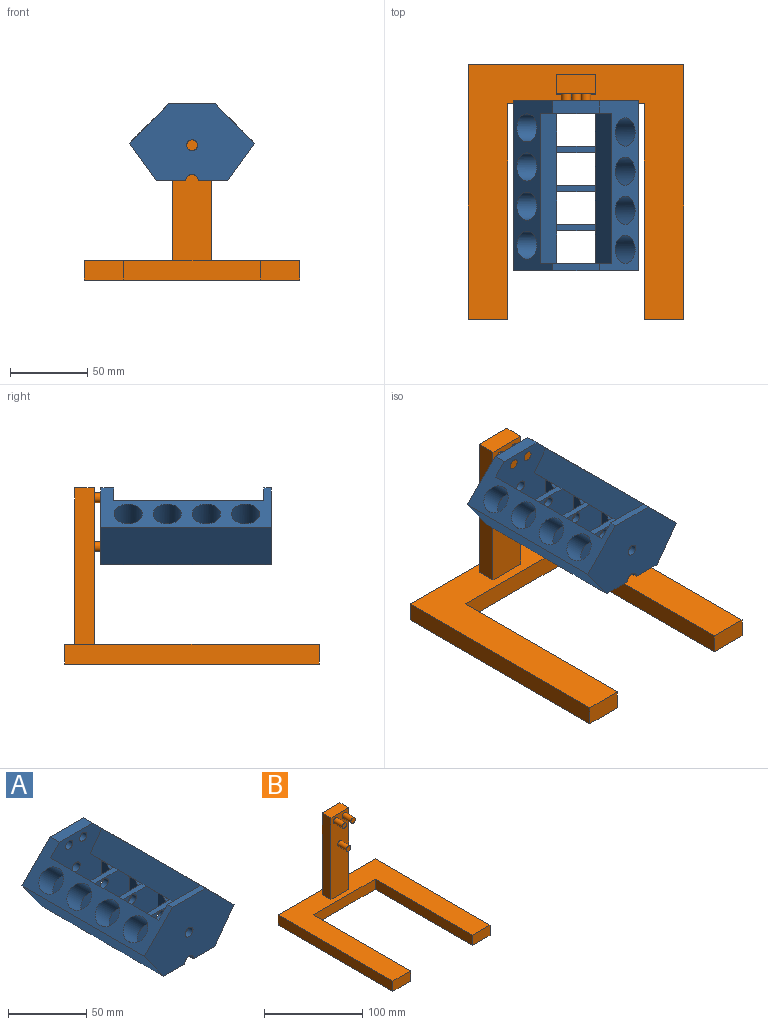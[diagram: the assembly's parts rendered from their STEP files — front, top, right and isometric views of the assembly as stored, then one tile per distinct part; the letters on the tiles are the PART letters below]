
ASSEMBLY  parts=2 mates=1
PART A: 64 faces, bbox 81.3x110.5x49.8 mm
  f0: plane 21.34x16.54mm, normal (-1,0,0), area 298.5mm2, adj f7,f11,f17,f51,f54
  f1: plane 21.34x16.54mm, normal (-1,0,0), area 298.5mm2, adj f8,f13,f17,f49,f56
  f2: plane 21.34x16.54mm, normal (-1,0,0), area 298.5mm2, adj f9,f10,f17,f52,f53
  f3: plane 21.34x16.54mm, normal (1,0,0), area 298.5mm2, adj f7,f11,f28,f47,f58
  f4: plane 21.34x16.54mm, normal (1,0,0), area 298.5mm2, adj f8,f13,f28,f45,f60
  f5: plane 21.34x16.54mm, normal (1,0,0), area 298.5mm2, adj f9,f10,f28,f48,f57
  f6: plane 49.81x46.33mm, normal (0,1,0), area 1910.8mm2, adj f14,f15,f17,f24,f25,f26,f27,f28
  f7: plane 46.33x27.08mm, normal (0,1,0), area 1077.7mm2, adj f0,f3,f17,f21,f28,f34,f39,f44
  f8: plane 46.33x27.08mm, normal (0,1,0), area 1077.7mm2, adj f1,f4,f17,f19,f28,f32,f37,f41
  f9: plane 46.33x27.08mm, normal (0,1,0), area 1077.7mm2, adj f2,f5,f17,f20,f28,f30,f35,f40
  f10: plane 46.33x27.08mm, normal (0,-1,0), area 1077.7mm2, adj f2,f5,f17,f19,f28,f32,f37,f41
  f11: plane 46.33x27.08mm, normal (0,-1,0), area 1077.7mm2, adj f0,f3,f17,f20,f28,f30,f35,f40
  f12: plane 46.33x27.08mm, normal (0,-1,0), area 1077.7mm2, adj f17,f21,f24,f27,f28,f34,f39,f44
  f13: plane 49.81x46.33mm, normal (0,-1,0), area 1815.8mm2, adj f1,f4,f14,f15,f17,f18,f22,f28
  f14: plane 110.49x25.61mm, normal (-0.71,0,0.71), area 1829mm2, adj f6,f13,f16,f22,f23,f25,f28,f42
  f15: plane 110.49x25.61mm, normal (0.71,0,0.71), area 1829mm2, adj f6,f13,f16,f22,f23,f25,f29,f43
  f16: plane 81.28x49.81mm, normal (0,-1,0), area 2904mm2, adj f14,f15,f17,f25,f26,f28,f29,f31
  f17: plane 110.49x19.1mm, normal (0,0,-1), area 480.3mm2, adj f0,f1,f2,f6,f7,f8,f9,f10
  f18: plane 19.1x8.38mm, normal (0,0,-1), area 160.1mm2, adj f13,f23,f28,f33
  f19: plane 19.1x4.06mm, normal (0,0,-1), area 77.6mm2, adj f8,f10,f28,f32
  f20: plane 19.1x4.06mm, normal (0,0,-1), area 77.6mm2, adj f9,f11,f28,f30
  f21: plane 19.1x4.06mm, normal (0,0,-1), area 77.6mm2, adj f7,f12,f28,f34
  f22: plane 30.06x8.38mm, normal (0,0,1), area 251.9mm2, adj f13,f14,f15,f23
  f23: plane 81.28x49.81mm, normal (0,1,0), area 2809mm2, adj f14,f15,f17,f18,f22,f28,f29,f33
  f24: plane 21.34x16.54mm, normal (-1,0,0), area 298.5mm2, adj f6,f12,f17,f50,f55
  f25: plane 30.06x4.57mm, normal (0,0,1), area 137.4mm2, adj f6,f14,f15,f16
  f26: plane 19.1x4.57mm, normal (0,0,-1), area 87.3mm2, adj f6,f16,f28,f31
  f27: plane 21.34x16.54mm, normal (1,0,0), area 298.5mm2, adj f6,f12,f28,f46,f59
  f28: plane 110.49x24.2mm, normal (-0.81,0,-0.59), area 3297.9mm2, adj f3,f4,f5,f6,f7,f8,f9,f10
  f29: plane 110.49x24.2mm, normal (0.81,0,-0.59), area 3297.9mm2, adj f15,f16,f17,f23
  f30: cylinder r=4.06mm len=8.13mm, axis (0,-1,0), area 51.9mm2, adj f9,f11,f17,f20
  f31: cylinder r=4.06mm len=8.13mm, axis (0,-1,0), area 58.4mm2, adj f6,f16,f17,f26
  f32: cylinder r=4.06mm len=8.13mm, axis (0,-1,0), area 51.9mm2, adj f8,f10,f17,f19
  f33: cylinder r=4.06mm len=8.38mm, axis (0,-1,0), area 107mm2, adj f13,f17,f18,f23
  f34: cylinder r=4.06mm len=8.13mm, axis (0,-1,0), area 51.9mm2, adj f7,f12,f17,f21
  f35: cylinder r=3.56mm len=7.11mm, axis (0,-1,0), area 90.8mm2, adj f9,f11
  f36: cylinder r=3.56mm len=7.11mm, axis (0,-1,0), area 102.2mm2, adj f6,f16
  f37: cylinder r=3.56mm len=7.11mm, axis (0,-1,0), area 90.8mm2, adj f8,f10
  f38: cylinder r=3.56mm len=8.38mm, axis (0,-1,0), area 187.3mm2, adj f13,f23
  f39: cylinder r=3.56mm len=7.11mm, axis (0,-1,0), area 90.8mm2, adj f7,f12
  f40: plane 25.25x4.06mm, normal (0,0,1), area 102.6mm2, adj f9,f11,f42,f43
  f41: plane 25.25x4.06mm, normal (0,0,1), area 102.6mm2, adj f8,f10,f42,f43
  f42: plane 97.54x14.6mm, normal (0.81,0,0.59), area 1756mm2, adj f6,f13,f14,f40,f41,f44,f45,f46
  f43: plane 97.54x14.6mm, normal (-0.81,0,0.59), area 1756.1mm2, adj f6,f13,f15,f40,f41,f44,f49,f50
  f44: plane 25.25x4.06mm, normal (0,0,1), area 102.6mm2, adj f7,f12,f42,f43
  f45: plane 21.34x10.54mm, normal (0.71,0,-0.71), area 93.8mm2, adj f4,f8,f13,f42,f60
  f46: plane 21.34x10.54mm, normal (0.71,0,-0.71), area 93.8mm2, adj f6,f12,f27,f42,f59
  f47: plane 21.34x10.54mm, normal (0.71,0,-0.71), area 93.8mm2, adj f3,f7,f11,f42,f58
  f48: plane 21.34x10.54mm, normal (0.71,0,-0.71), area 93.8mm2, adj f5,f9,f10,f42,f57
  f49: plane 21.34x10.54mm, normal (-0.71,0,-0.71), area 93.8mm2, adj f1,f8,f13,f43,f56
  f50: plane 21.34x10.54mm, normal (-0.71,0,-0.71), area 93.8mm2, adj f6,f12,f24,f43,f55
  f51: plane 21.34x10.54mm, normal (-0.71,0,-0.71), area 93.8mm2, adj f0,f7,f11,f43,f54
  f52: plane 21.34x10.54mm, normal (-0.71,0,-0.71), area 93.8mm2, adj f2,f9,f10,f43,f53
  f53: cylinder r=9.14mm len=28.14mm, axis (0.71,0,0.71), area 1063.1mm2, adj f2,f15,f52
  f54: cylinder r=9.14mm len=28.14mm, axis (0.71,0,0.71), area 1063.1mm2, adj f0,f15,f51
  f55: cylinder r=9.14mm len=28.14mm, axis (0.71,0,0.71), area 1063.1mm2, adj f15,f24,f50
  f56: cylinder r=9.14mm len=28.14mm, axis (0.71,0,0.71), area 1063.1mm2, adj f1,f15,f49
  f57: cylinder r=9.14mm len=28.14mm, axis (-0.71,0,0.71), area 1063.1mm2, adj f5,f14,f48
  f58: cylinder r=9.14mm len=28.14mm, axis (-0.71,0,0.71), area 1063.1mm2, adj f3,f14,f47
  f59: cylinder r=9.14mm len=28.14mm, axis (-0.71,0,0.71), area 1063.1mm2, adj f14,f27,f46
  f60: cylinder r=9.14mm len=28.14mm, axis (-0.71,0,0.71), area 1063.1mm2, adj f4,f14,f45
  f61: cylinder r=3.17mm len=8.38mm, axis (0,1,0), area 167.2mm2, adj f13,f23
  f62: cylinder r=3.17mm len=8.38mm, axis (0,1,0), area 167.2mm2, adj f13,f23
  f63: cylinder r=3.17mm len=8.38mm, axis (0,1,0), area 167.2mm2, adj f13,f23
PART B: 21 faces, bbox 139.7x165.1x114.3 mm
  f0: plane 165.1x139.7mm, normal (0,0,1), area 10322.6mm2, adj f1,f2,f4,f5,f6,f7,f8,f9
  f1: plane 88.9x12.7mm, normal (0,-1,0), area 1129mm2, adj f0,f2,f3,f7
  f2: plane 139.7x12.7mm, normal (-1,0,0), area 1774.2mm2, adj f0,f1,f3,f5
  f3: plane 165.1x139.7mm, normal (0,0,-1), area 10645.1mm2, adj f1,f2,f4,f5,f6,f7,f8,f9
  f4: plane 165.1x12.7mm, normal (1,0,0), area 2096.8mm2, adj f0,f3,f5,f9
  f5: plane 25.4x12.7mm, normal (0,-1,0), area 322.6mm2, adj f0,f2,f3,f4
  f6: plane 165.1x12.7mm, normal (-1,0,0), area 2096.8mm2, adj f0,f3,f8,f9
  f7: plane 139.7x12.7mm, normal (1,0,0), area 1774.2mm2, adj f0,f1,f3,f8
  f8: plane 25.4x12.7mm, normal (0,-1,0), area 322.6mm2, adj f0,f3,f6,f7
  f9: plane 139.7x12.7mm, normal (0,1,0), area 1774.2mm2, adj f0,f3,f4,f6
  f10: plane 101.6x12.7mm, normal (1,0,0), area 1290.3mm2, adj f0,f11,f13,f14
  f11: plane 101.6x25.4mm, normal (0,1,0), area 2580.6mm2, adj f0,f10,f12,f14
  f12: plane 101.6x12.7mm, normal (-1,0,0), area 1290.3mm2, adj f0,f11,f13,f14
  f13: plane 101.6x25.4mm, normal (0,-1,0), area 2485.6mm2, adj f0,f10,f12,f14,f15,f17,f19
  f14: plane 25.4x12.7mm, normal (0,0,1), area 322.6mm2, adj f10,f11,f12,f13
  f15: cylinder r=3.17mm len=12.7mm, axis (0,1,0), area 253.4mm2, adj f13,f16
  f16: plane 6.35x6.35mm, normal (0,-1,0), area 31.7mm2, adj f15
  f17: cylinder r=3.17mm len=12.7mm, axis (0,1,0), area 253.4mm2, adj f13,f18
  f18: plane 6.35x6.35mm, normal (0,-1,0), area 31.7mm2, adj f17
  f19: cylinder r=3.17mm len=12.7mm, axis (0,1,0), area 253.4mm2, adj f13,f20
  f20: plane 6.35x6.35mm, normal (0,-1,0), area 31.7mm2, adj f19
PLACE A t=(-86.84,-41.65,-74.64)mm
PLACE B t=(-49.92,41.55,-132.78)mm
MATE fastened B.f15 <-> A.f61  axis (0,-1,0) through (-62.62,22.5,-31.18)mm
